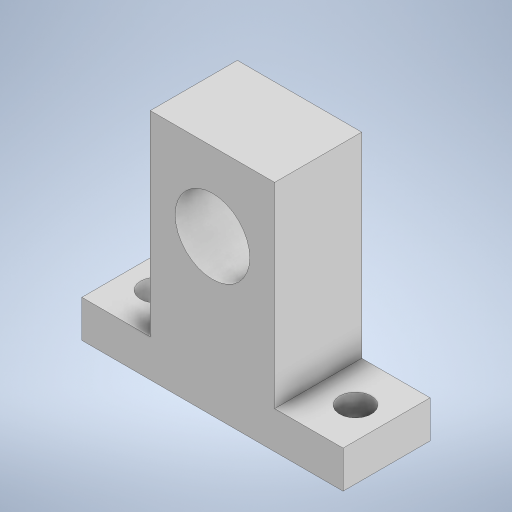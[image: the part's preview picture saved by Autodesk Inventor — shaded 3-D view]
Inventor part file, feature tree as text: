
AUTODESK INVENTOR PART (.ipt)
format: ipt  version: 2023.2 (Build 272271000, 271)  size: 240,128 bytes
history: native  units: mm
features: sketch x2, extrude x1, hole x1
ambient origin geometry x8: Origin, YZ Plane, XZ Plane, XY Plane, X Axis, Y Axis, Z Axis, Center Point
bodies: Solid1 (feature_tree)
feature tree (4):
  extrude  "Extrusion1"  Depth=31.5mm
  hole  "Hole1"  [1 undecoded]
  sketch  "Sketch1"  dims[d0=20.0mm d1=31.5mm]
  sketch  "Sketch2"  dims[d2=6.0mm d3=42.0mm d4=11.0mm d5=12.0mm d6=25.0mm d7=14.0mm d8=0.0mm d9=5.0mm d10=5.0mm d11=5.1mm d12=6.0mm d13=19.05mm d14=4.775mm d15=90.0deg d16=8.0mm d17=20.594885mm]
note: 1 required parameter value undecoded (feature->parameter linkage not recoverable at this tier; creation-order binding heuristic only, values carry confidence <= 0.55)
